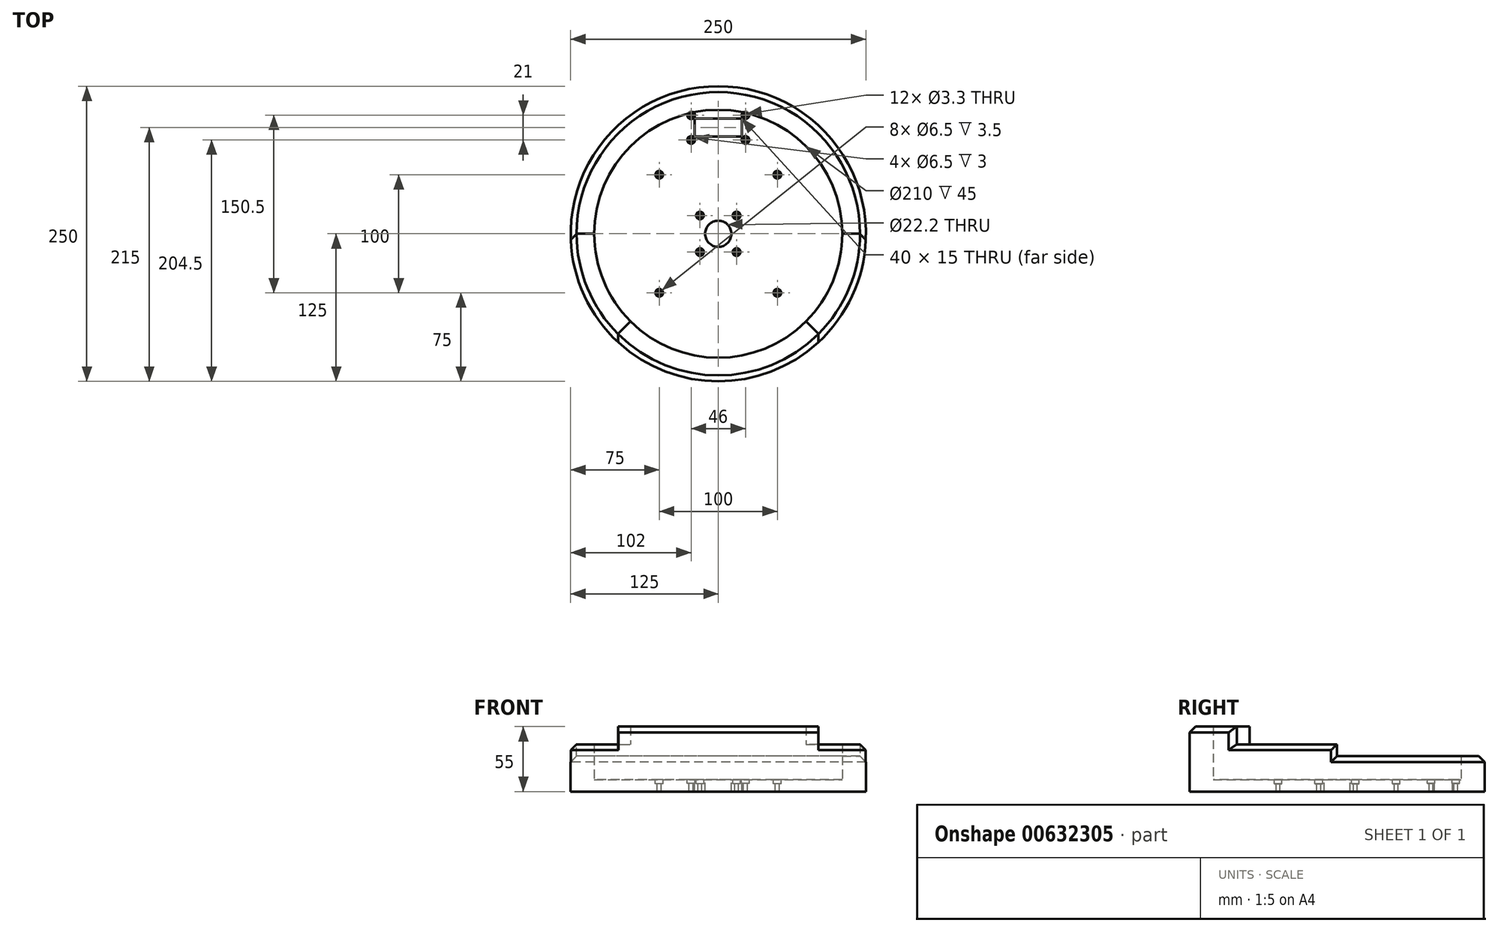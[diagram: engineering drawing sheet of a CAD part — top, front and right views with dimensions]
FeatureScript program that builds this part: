
annotation { "Feature Type Name" : "Feature", "Feature Type Description" : "" }
export const myFeature = defineFeature(function(context is Context, id is Id, definition is map)
    precondition{}
    {
        {
            var Q0;
            Q0=qCreatedBy(makeId("Top.planeOp"),FACE);
            var sketch = newSketch(context, id + "F0", { "sketchPlane" : qUnion([Q0])});
            skCircle(sketch, "E0", {"center": v(0, 0) * mm, "radius": 125 * mm});
            skSolve(sketch);
        }
        {
            var Q0;
            Q0=makeQuery(id+"F0.imprint","IMPRINT",FACE,{"disambiguationData":[TD([[makeQuery(id+"F0.imprint","IMPRINT",EDGE,{"derivedFrom":sQuery(id+"F0.wireOp",EDGE,"E0")}),1.0]])]});
            extrude(context, id + "F1", {"entities" : qUnion([Q0]), "depth" : 10 * mm, "offsetDistance" : 25 * mm});
        }
        {
            var Q0;
            Q0=makeQuery(id+"F1.opExtrude","CAP_FACE",FACE,{"disambiguationData":[OSD([sQuery(id+"F0.wireOp",EDGE,"E0")])],"isStart":false});
            var sketch = newSketch(context, id + "F2", { "sketchPlane" : qUnion([Q0])});
            skCircle(sketch, "E1", {"center": v(0, 0) * mm, "radius": 105 * mm});
            skCircle(sketch, "E2", {"center": v(0, 0) * mm, "radius": 11.1 * mm});
            skLineSegment(sketch, "E3.bottom", {"start": v(15.5, -15.5) * mm, "end": v(-15.5, -15.5) * mm, "construction": true});
            skLineSegment(sketch, "E3.top", {"start": v(15.5, 15.5) * mm, "end": v(-15.5, 15.5) * mm, "construction": true});
            skLineSegment(sketch, "E3.left", {"start": v(15.5, -15.5) * mm, "end": v(15.5, 15.5) * mm, "construction": true});
            skLineSegment(sketch, "E3.right", {"start": v(-15.5, -15.5) * mm, "end": v(-15.5, 15.5) * mm, "construction": true});
            skPoint(sketch, "E4", {"position": v(-15.5, 15.5) * mm});
            skPoint(sketch, "E5", {"position": v(15.5, 15.5) * mm});
            skPoint(sketch, "E6", {"position": v(15.5, -15.5) * mm});
            skPoint(sketch, "E7", {"position": v(-15.5, -15.5) * mm});
            skLineSegment(sketch, "E8.bottom", {"start": v(20, 82.5) * mm, "end": v(-20, 82.5) * mm});
            skLineSegment(sketch, "E8.top", {"start": v(20, 97.5) * mm, "end": v(-20, 97.5) * mm});
            skLineSegment(sketch, "E8.left", {"start": v(20, 82.5) * mm, "end": v(20, 97.5) * mm});
            skLineSegment(sketch, "E8.right", {"start": v(-20, 82.5) * mm, "end": v(-20, 97.5) * mm});
            skPoint(sketch, "E8.middle", {"position": v(0, 90) * mm});
            skLineSegment(sketch, "E9.bottom", {"start": v(50, -50) * mm, "end": v(-50, -50) * mm, "construction": true});
            skLineSegment(sketch, "E9.top", {"start": v(50, 50) * mm, "end": v(-50, 50) * mm, "construction": true});
            skLineSegment(sketch, "E9.left", {"start": v(50, -50) * mm, "end": v(50, 50) * mm, "construction": true});
            skLineSegment(sketch, "E9.right", {"start": v(-50, -50) * mm, "end": v(-50, 50) * mm, "construction": true});
            skPoint(sketch, "E10", {"position": v(-50, 50) * mm});
            skPoint(sketch, "E11", {"position": v(50, 50) * mm});
            skPoint(sketch, "E12", {"position": v(50, -50) * mm});
            skPoint(sketch, "E13", {"position": v(-50, -50) * mm});
            skLineSegment(sketch, "E14.bottom", {"start": v(23, 79.5) * mm, "end": v(-23, 79.5) * mm, "construction": true});
            skLineSegment(sketch, "E14.top", {"start": v(23, 100.5) * mm, "end": v(-23, 100.5) * mm, "construction": true});
            skLineSegment(sketch, "E14.left", {"start": v(23, 79.5) * mm, "end": v(23, 100.5) * mm, "construction": true});
            skLineSegment(sketch, "E14.right", {"start": v(-23, 79.5) * mm, "end": v(-23, 100.5) * mm, "construction": true});
            skPoint(sketch, "E15", {"position": v(-23, 100.5) * mm});
            skPoint(sketch, "E16", {"position": v(23, 100.5) * mm});
            skPoint(sketch, "E17", {"position": v(23, 79.5) * mm});
            skPoint(sketch, "E18", {"position": v(-23, 79.5) * mm});
            skSolve(sketch);
        }
        {
            var Q0;
            Q0=makeQuery(id+"F2.imprint","IMPRINT",FACE,{"disambiguationData":[TD([[makeQuery(id+"F2.imprint","IMPRINT",EDGE,{"derivedFrom":sQuery(id+"F2.wireOp",EDGE,"E1")}),-1.0]])]});
            extrude(context, id + "F3", {"entities" : qUnion([Q0]), "operationType" : NewBodyOperationType.ADD, "depth" : 20 * mm, "offsetDistance" : 25 * mm});
        }
        {
            var Q0;
            Q0=makeQuery(id+"F2.imprint","IMPRINT",FACE,{"disambiguationData":[TD([[makeQuery(id+"F2.imprint","IMPRINT",EDGE,{"derivedFrom":sQuery(id+"F2.wireOp",EDGE,"E2")}),1.0]])]});
            var Q1;
            Q1=makeQuery(id+"F2.imprint","IMPRINT",FACE,{"disambiguationData":[TD([[makeQuery(id+"F2.imprint","IMPRINT",EDGE,{"derivedFrom":sQuery(id+"F2.wireOp",EDGE,"E8.bottom")}),-1.0]])]});
            extrude(context, id + "F4", {"entities" : qUnion([Q0, Q1]), "operationType" : NewBodyOperationType.REMOVE, "oppositeDirection" : true, "depth" : 10 * mm, "offsetDistance" : 25 * mm});
        }
        {
            var Q0;
            Q0=makeQuery(id+"F3.opExtrude","CAP_FACE",FACE,{"disambiguationData":[OSD([sQuery(id+"F0.wireOp",EDGE,"E0"),sQuery(id+"F2.wireOp",EDGE,"E1")])],"isStart":false});
            var sketch = newSketch(context, id + "F5", { "sketchPlane" : qUnion([Q0])});
            skLineSegment(sketch, "E19", {"start": v(0, 0) * mm, "end": v(-74.25, -74.25) * mm, "construction": true});
            skLineSegment(sketch, "E20", {"start": v(-88.39, -88.39) * mm, "end": v(-74.25, -74.25) * mm});
            skLineSegment(sketch, "E21.MirrorCS", {"start": v(88.39, -88.39) * mm, "end": v(74.25, -74.25) * mm});
            skLineSegment(sketch, "E22", {"start": v(0, 0) * mm, "end": v(-105, 0) * mm, "construction": true});
            skLineSegment(sketch, "E23", {"start": v(-105, 0) * mm, "end": v(-125, 0) * mm});
            skLineSegment(sketch, "E24.MirrorCS", {"start": v(105, 0) * mm, "end": v(125, 0) * mm});
            skSolve(sketch);
        }
        {
            var Q0;
            Q0=sQuery(id+"F2.wireOp",VERTEX,"E4");
            var Q1;
            Q1=sQuery(id+"F2.wireOp",VERTEX,"E5");
            var Q2;
            Q2=sQuery(id+"F2.wireOp",VERTEX,"E6");
            var Q3;
            Q3=sQuery(id+"F2.wireOp",VERTEX,"E7");
            var Q4;
            Q4=sQuery(id+"F2.wireOp",VERTEX,"E10");
            var Q5;
            Q5=sQuery(id+"F2.wireOp",VERTEX,"E11");
            var Q6;
            Q6=sQuery(id+"F2.wireOp",VERTEX,"E12");
            var Q7;
            Q7=sQuery(id+"F2.wireOp",VERTEX,"E13");
            var Q8;
            Q8=makeQuery(id+"F1.opExtrude","SWEPT_BODY",BODY,{"disambiguationData":[OSD([sQuery(id+"F0.wireOp",EDGE,"E0")])]});
            hole(context, id + "F6", {"style" : HoleStyle.C_BORE, "endStyle" : HoleEndStyle.THROUGH, "holeDiameter" : 3.3 * mm, "cBoreDiameter" : 6.5 * mm, "cBoreDepth" : 3.5 * mm, "majorDiameter" : 5 * mm, "isTappedThrough" : true, "tappedDepth" : 12 * mm, "tapClearance" : 3, "locations" : qUnion([Q0, Q1, Q2, Q3, Q4, Q5, Q6, Q7]), "scope" : qUnion([Q8])});
        }
        {
            var Q0;
            Q0 = qSketchRegion(id + "F5", true);
            var Q1;
            {var subQ0=sQuery(id+"F5.wireOp",EDGE,"E20");Q1=makeQuery(id+"F5.imprint","IMPRINT",FACE,{"disambiguationData":[TD([[makeQuery(id+"F5.imprint","IMPRINT",EDGE,{"derivedFrom":subQ0}),-1.0]])]});}
            extrude(context, id + "F7", {"entities" : qUnion([Q0, Q1]), "operationType" : NewBodyOperationType.ADD, "depth" : 25 * mm, "offsetDistance" : 25 * mm});
        }
        {
            var Q0;
            {var subQ0=sQuery(id+"F5.wireOp",EDGE,"E20");Q0=makeQuery(id+"F5.imprint","IMPRINT",FACE,{"disambiguationData":[TD([[makeQuery(id+"F5.imprint","IMPRINT",EDGE,{"derivedFrom":subQ0}),1.0]])]});}
            var Q1;
            {var subQ0=sQuery(id+"F5.wireOp",EDGE,"E21.MirrorCS");Q1=makeQuery(id+"F5.imprint","IMPRINT",FACE,{"disambiguationData":[TD([[makeQuery(id+"F5.imprint","IMPRINT",EDGE,{"derivedFrom":subQ0}),-1.0]])]});}
            extrude(context, id + "F8", {"entities" : qUnion([Q0, Q1]), "operationType" : NewBodyOperationType.ADD, "depth" : 10 * mm, "offsetDistance" : 25 * mm});
        }
        {
            var Q0;
            Q0=sQuery(id+"F2.wireOp",VERTEX,"E15");
            var Q1;
            Q1=sQuery(id+"F2.wireOp",VERTEX,"E18");
            var Q2;
            Q2=sQuery(id+"F2.wireOp",VERTEX,"E17");
            var Q3;
            Q3=sQuery(id+"F2.wireOp",VERTEX,"E16");
            var Q4;
            Q4=makeQuery(id+"F1.opExtrude","SWEPT_BODY",BODY,{"disambiguationData":[OSD([sQuery(id+"F0.wireOp",EDGE,"E0")])]});
            hole(context, id + "F9", {"style" : HoleStyle.C_BORE, "endStyle" : HoleEndStyle.THROUGH, "standardTappedOrClearance" : lookupTablePath({ "standard" : "ISO", "fit" : "Normal", "size" : "M3", "type" : "Clearance" }), "standardBlindInLast" : lookupTablePath({ "fit" : "Standard", "standard" : "ISO", "size" : "M3", "type" : "Clearance" }), "holeDiameter" : 3.3 * mm, "cBoreDiameter" : 6.5 * mm, "cBoreDepth" : 3 * mm, "majorDiameter" : 5 * mm, "isTappedThrough" : true, "tappedDepth" : 12 * mm, "tapClearance" : 3, "locations" : qUnion([Q0, Q1, Q2, Q3]), "scope" : qUnion([Q4])});
        }
        {
            var Q0;
            Q0=makeQuery(id+"F3.opExtrude","CAP_EDGE",EDGE,{"disambiguationData":[OSD([sQuery(id+"F0.wireOp",EDGE,"E0")])],"isStart":false});
            var Q1;
            {var subQ0=sQuery(id+"F0.wireOp",EDGE,"E0");var subQ1=makeQuery(id+"F3.opExtrude","CAP_EDGE",EDGE,{"disambiguationData":[OSD([subQ0])],"isStart":false});Q1=makeQuery(id+"F8.opExtrude","CAP_EDGE",EDGE,{"disambiguationData":[OSD([subQ0]),TDD([makeQuery(id+"F5.imprint","IMPRINT",EDGE,{"disambiguationData":[TD([[makeQuery(id+"F5.imprint","INTERSECT",VERTEX,{"derivedFrom":[subQ1,sQuery(id+"F5.wireOp",EDGE,"E20")]}),1.0]])],"derivedFrom":subQ1})])],"isStart":false});}
            var Q2;
            Q2=makeQuery(id+"F8.opExtrude","SWEPT_EDGE",EDGE,{"disambiguationData":[OSD([sQuery(id+"F0.wireOp",EDGE,"E0"),sQuery(id+"F5.wireOp",EDGE,"E23")])]});
            var Q3;
            Q3=makeQuery(id+"F7.opExtrude","CAP_EDGE",EDGE,{"disambiguationData":[OSD([sQuery(id+"F0.wireOp",EDGE,"E0")])],"isStart":false});
            var Q4;
            Q4=makeQuery(id+"F7.opExtrude","SWEPT_EDGE",EDGE,{"disambiguationData":[OSD([sQuery(id+"F0.wireOp",EDGE,"E0"),sQuery(id+"F5.wireOp",EDGE,"E20")])]});
            var Q5;
            Q5=makeQuery(id+"F7.opExtrude","SWEPT_EDGE",EDGE,{"disambiguationData":[OSD([sQuery(id+"F0.wireOp",EDGE,"E0"),sQuery(id+"F5.wireOp",EDGE,"E21.MirrorCS")])]});
            var Q6;
            {var subQ0=sQuery(id+"F0.wireOp",EDGE,"E0");var subQ1=makeQuery(id+"F3.opExtrude","CAP_EDGE",EDGE,{"disambiguationData":[OSD([subQ0])],"isStart":false});Q6=makeQuery(id+"F8.opExtrude","CAP_EDGE",EDGE,{"disambiguationData":[OSD([subQ0]),TDD([makeQuery(id+"F5.imprint","IMPRINT",EDGE,{"disambiguationData":[TD([[makeQuery(id+"F5.imprint","INTERSECT",VERTEX,{"derivedFrom":[subQ1,sQuery(id+"F5.wireOp",EDGE,"E21.MirrorCS")]}),-1.0]])],"derivedFrom":subQ1})])],"isStart":false});}
            var Q7;
            Q7=makeQuery(id+"F8.opExtrude","SWEPT_EDGE",EDGE,{"disambiguationData":[OSD([sQuery(id+"F0.wireOp",EDGE,"E0"),sQuery(id+"F5.wireOp",EDGE,"E24.MirrorCS")])]});
            chamfer(context, id + "F10", {"entities" : qUnion([Q0, Q1, Q2, Q3, Q4, Q5, Q6, Q7]), "width" : 5 * mm, "tangentPropagation" : true});
        }
    });
